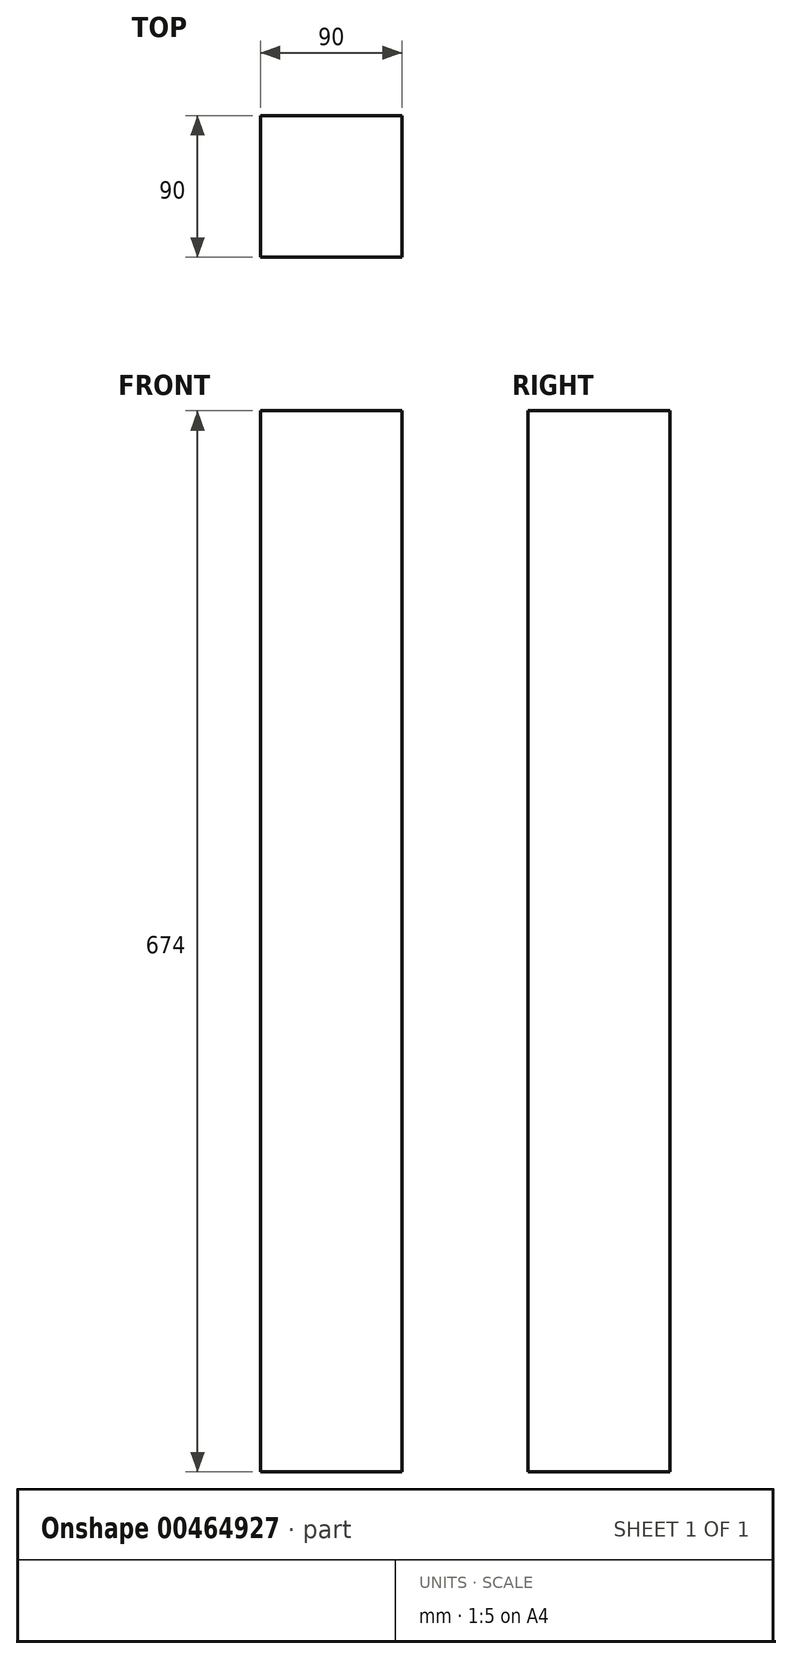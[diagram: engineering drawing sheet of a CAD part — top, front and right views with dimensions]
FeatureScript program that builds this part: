
annotation { "Feature Type Name" : "Feature", "Feature Type Description" : "" }
export const myFeature = defineFeature(function(context is Context, id is Id, definition is map)
    precondition{}
    {
        {
            var Q0;
            Q0=qCreatedBy(makeId("Top.planeOp"),FACE);
            var sketch = newSketch(context, id + "F0", { "sketchPlane" : qUnion([Q0])});
            skLineSegment(sketch, "E0.bottom", {"start": v(45, -45) * mm, "end": v(-45, -45) * mm});
            skLineSegment(sketch, "E0.top", {"start": v(45, 45) * mm, "end": v(-45, 45) * mm});
            skLineSegment(sketch, "E0.left", {"start": v(45, -45) * mm, "end": v(45, 45) * mm});
            skLineSegment(sketch, "E0.right", {"start": v(-45, -45) * mm, "end": v(-45, 45) * mm});
            skPoint(sketch, "E0.middle", {"position": v(0, 0) * mm});
            skSolve(sketch);
        }
        {
            var Q0;
            Q0=makeQuery(id+"F0.imprint","IMPRINT",FACE,{"disambiguationData":[TD([[makeQuery(id+"F0.imprint","IMPRINT",EDGE,{"derivedFrom":sQuery(id+"F0.wireOp",EDGE,"E0.bottom")}),-1.0]])]});
            extrude(context, id + "F1", {"entities" : qUnion([Q0]), "oppositeDirection" : true, "depth" : (550 + 124) * mm, "offsetDistance" : 25 * mm});
        }
    });
